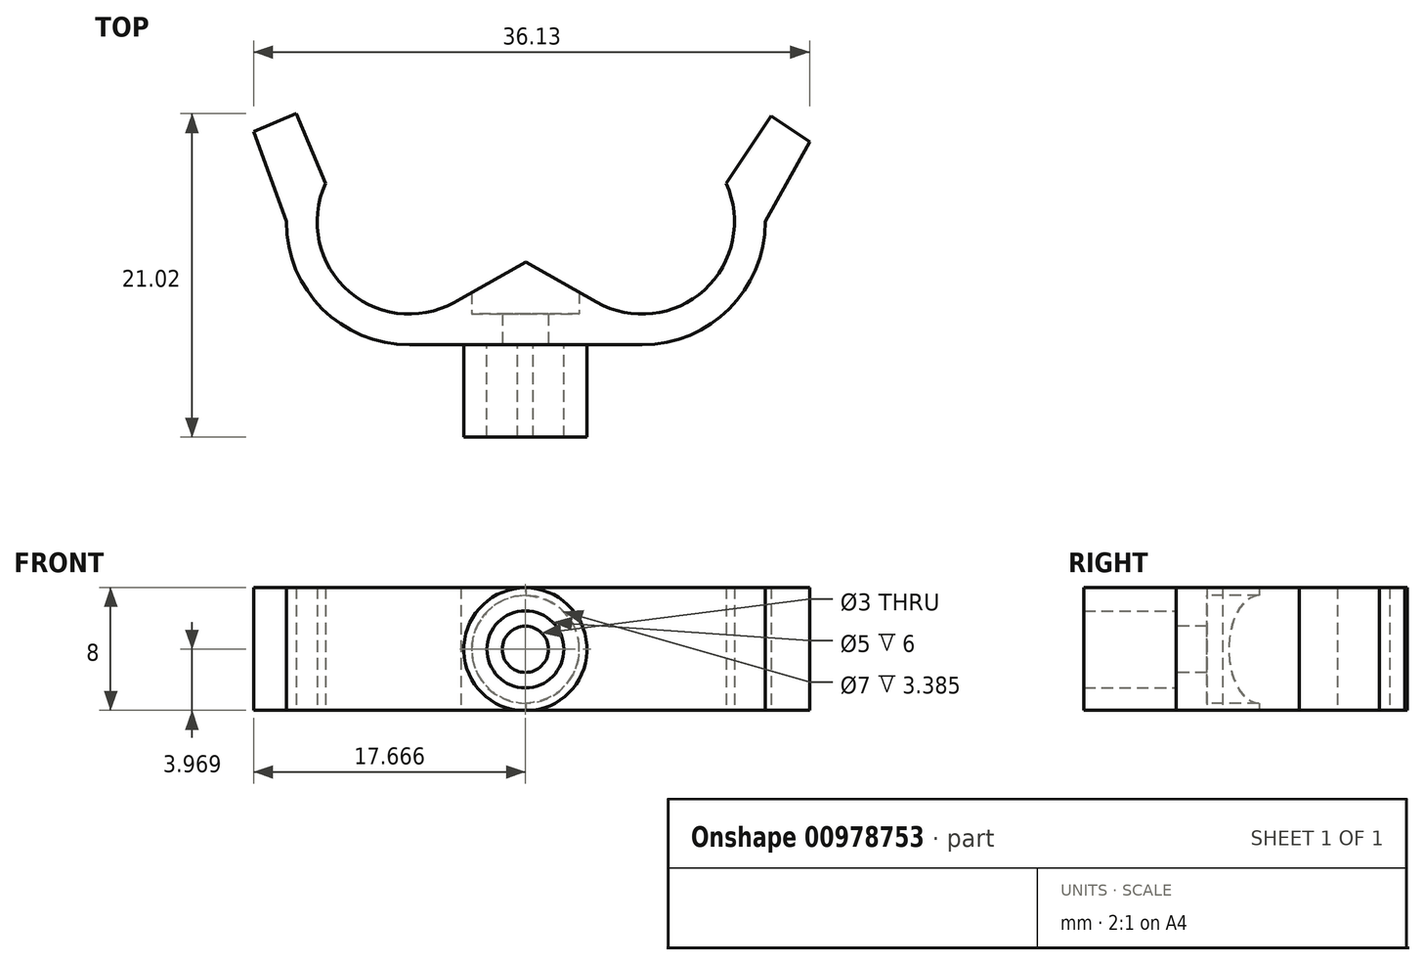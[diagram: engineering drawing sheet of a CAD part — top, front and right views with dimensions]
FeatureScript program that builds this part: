
annotation { "Feature Type Name" : "Feature", "Feature Type Description" : "" }
export const myFeature = defineFeature(function(context is Context, id is Id, definition is map)
    precondition{}
    {
        {
            var Q0;
            Q0=qCreatedBy(makeId("Top.planeOp"),FACE);
            var sketch = newSketch(context, id + "F0", { "sketchPlane" : qUnion([Q0])});
            skCircle(sketch, "E0", {"center": v(0, 0) * mm, "radius": 8 * mm});
            skCircle(sketch, "E1", {"center": v(15.12, 0) * mm, "radius": 8 * mm});
            skLineSegment(sketch, "E2", {"start": v(0, -8) * mm, "end": v(15.12, -8) * mm});
            skCircle(sketch, "E3", {"center": v(0, 0) * mm, "radius": 6 * mm});
            skCircle(sketch, "E4", {"center": v(15.12, 0) * mm, "radius": 6 * mm});
            skLineSegment(sketch, "E5", {"start": v(-5.46, 2.49) * mm, "end": v(-7.37, 7.02) * mm});
            skLineSegment(sketch, "E6", {"start": v(-7.37, 7.02) * mm, "end": v(-10.13, 5.86) * mm});
            skLineSegment(sketch, "E7", {"start": v(-10.13, 5.86) * mm, "end": v(-8, 0) * mm});
            skLineSegment(sketch, "E8", {"start": v(20.58, 2.49) * mm, "end": v(23.51, 6.86) * mm});
            skLineSegment(sketch, "E9", {"start": v(23.51, 6.86) * mm, "end": v(26, 5.19) * mm});
            skLineSegment(sketch, "E10", {"start": v(26, 5.19) * mm, "end": v(23.12, 0) * mm});
            skLineSegment(sketch, "E11", {"start": v(7.56, -2.62) * mm, "end": v(3.34, -4.99) * mm});
            skLineSegment(sketch, "E12", {"start": v(7.56, -2.62) * mm, "end": v(12.17, -5.22) * mm});
            skSolve(sketch);
        }
        {
            var Q0;
            {var subQ2=sQuery(id+"F0.wireOp",EDGE,"E11");Q0=makeQuery(id+"F0.imprint","IMPRINT",FACE,{"disambiguationData":[TD([[makeQuery(id+"F0.imprint","IMPRINT",EDGE,{"derivedFrom":subQ2}),1.0]])]});}
            var Q1;
            {var subQ0=sQuery(id+"F0.wireOp",EDGE,"E2");Q1=makeQuery(id+"F0.imprint","IMPRINT",FACE,{"disambiguationData":[TD([[makeQuery(id+"F0.imprint","IMPRINT",EDGE,{"derivedFrom":subQ0}),1.0]])]});}
            var Q2;
            {var subQ3=sQuery(id+"F0.wireOp",EDGE,"E12");Q2=makeQuery(id+"F0.imprint","IMPRINT",FACE,{"disambiguationData":[TD([[makeQuery(id+"F0.imprint","IMPRINT",EDGE,{"derivedFrom":subQ3}),-1.0]])]});}
            var Q3;
            {var subQ4=sQuery(id+"F0.wireOp",EDGE,"E9");Q3=makeQuery(id+"F0.imprint","IMPRINT",FACE,{"disambiguationData":[TD([[makeQuery(id+"F0.imprint","IMPRINT",EDGE,{"derivedFrom":subQ4}),-1.0]])]});}
            var Q4;
            {var subQ4=sQuery(id+"F0.wireOp",EDGE,"E6");Q4=makeQuery(id+"F0.imprint","IMPRINT",FACE,{"disambiguationData":[TD([[makeQuery(id+"F0.imprint","IMPRINT",EDGE,{"derivedFrom":subQ4}),1.0]])]});}
            extrude(context, id + "F1", {"entities" : qUnion([Q0, Q1, Q2, Q3, Q4]), "depth" : 8 * mm, "offsetDistance" : 25 * mm});
        }
        {
            var Q0;
            Q0=makeQuery(id+"F1.opExtrude","SWEPT_FACE",FACE,{"disambiguationData":[OSD([sQuery(id+"F0.wireOp",EDGE,"E2")])]});
            var sketch = newSketch(context, id + "F2", { "sketchPlane" : qUnion([Q0])});
            skCircle(sketch, "E13", {"center": v(7.54, 3.97) * mm, "radius": 1.5 * mm});
            skCircle(sketch, "E14", {"center": v(7.54, 3.97) * mm, "radius": 4 * mm});
            skCircle(sketch, "E15", {"center": v(7.54, 3.97) * mm, "radius": 2.5 * mm});
            skSolve(sketch);
        }
        {
            var Q0;
            Q0=makeQuery(id+"F2.imprint","IMPRINT",FACE,{"disambiguationData":[TD([[makeQuery(id+"F2.imprint","IMPRINT",EDGE,{"derivedFrom":sQuery(id+"F2.wireOp",EDGE,"E13")}),1.0]])]});
            extrude(context, id + "F3", {"entities" : qUnion([Q0]), "operationType" : NewBodyOperationType.REMOVE, "oppositeDirection" : true, "depth" : 25 * mm, "offsetDistance" : 25 * mm});
        }
        {
            var Q0;
            Q0=makeQuery(id+"F2.imprint","IMPRINT",FACE,{"disambiguationData":[TD([[makeQuery(id+"F2.imprint","IMPRINT",EDGE,{"derivedFrom":sQuery(id+"F2.wireOp",EDGE,"E15")}),-1.0]])]});
            extrude(context, id + "F4", {"entities" : qUnion([Q0]), "operationType" : NewBodyOperationType.ADD, "depth" : 6 * mm, "offsetDistance" : 25 * mm});
        }
        {
            var Q0;
            Q0=makeQuery(id+"F2.imprint","IMPRINT",FACE,{"disambiguationData":[TD([[makeQuery(id+"F2.imprint","IMPRINT",EDGE,{"derivedFrom":sQuery(id+"F2.wireOp",EDGE,"E13")}),-1.0]])]});
            var sketch = newSketch(context, id + "F5", { "sketchPlane" : qUnion([Q0])});
            skCircle(sketch, "E16", {"center": v(7.54, 3.97) * mm, "radius": 3.5 * mm});
            skSolve(sketch);
        }
        {
            var Q0;
            Q0 = qSketchRegion(id + "F5", true);
            extrude(context, id + "F6", {"entities" : qUnion([Q0]), "operationType" : NewBodyOperationType.REMOVE, "oppositeDirection" : true, "depth" : 25 * mm, "offsetDistance" : 25 * mm, "hasSecondDirection" : true, "secondDirectionOppositeDirection" : true, "secondDirectionDepth" : 2 * mm});
        }
    });
